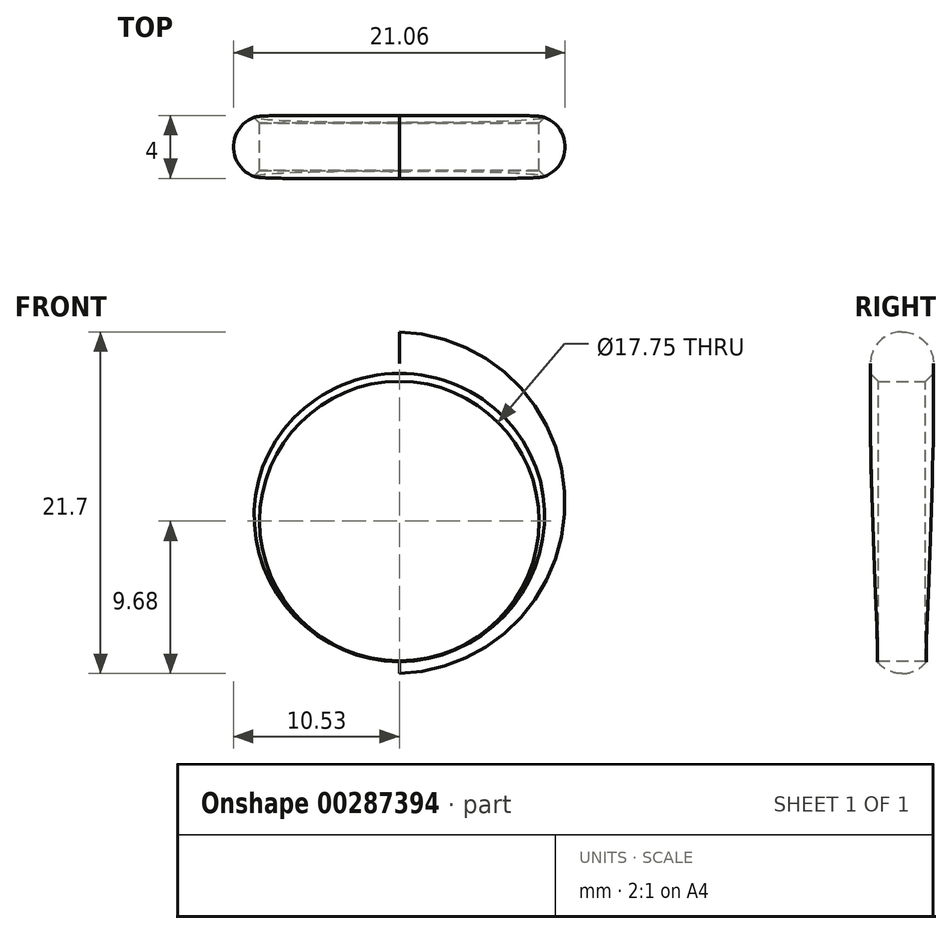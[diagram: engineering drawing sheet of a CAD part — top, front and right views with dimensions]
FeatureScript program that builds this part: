
annotation { "Feature Type Name" : "Feature", "Feature Type Description" : "" }
export const myFeature = defineFeature(function(context is Context, id is Id, definition is map)
    precondition{}
    {
        {
            var Q0;
            Q0=qCreatedBy(makeId("Front.planeOp"),FACE);
            var sketch = newSketch(context, id + "F0", { "sketchPlane" : qUnion([Q0])});
            skCircle(sketch, "E0", {"center": v(0, 0) * mm, "radius": 8.88 * mm});
            skPoint(sketch, "E1", {"position": v(0, 12.02) * mm});
            skPoint(sketch, "E2", {"position": v(0, -9.68) * mm});
            skArc(sketch, "E3", {"start": v(0, 12.02) * mm, "mid": v(-10.53, 1.17) * mm, "end": v(0, -9.68) * mm});
            skArc(sketch, "E4.MirrorCS", {"start": v(0, 12.02) * mm, "mid": v(10.53, 1.17) * mm, "end": v(0, -9.68) * mm});
            skPoint(sketch, "E5", {"position": v(-10.52, 10.9) * mm});
            skPoint(sketch, "E6", {"position": v(0, 15.2) * mm});
            skArc(sketch, "E7", {"start": v(0, 15.2) * mm, "mid": v(-5.65, 14) * mm, "end": v(-10.52, 10.9) * mm});
            skArc(sketch, "E8", {"start": v(-10.52, 10.9) * mm, "mid": v(-11.14, 8.31) * mm, "end": v(-9.01, 6.7) * mm});
            skArc(sketch, "E9.MirrorCS", {"start": v(0, 15.2) * mm, "mid": v(5.65, 14) * mm, "end": v(10.52, 10.9) * mm});
            skArc(sketch, "E10.MirrorCS", {"start": v(10.52, 10.9) * mm, "mid": v(11.14, 8.31) * mm, "end": v(9.01, 6.7) * mm});
            skSolve(sketch);
        }
        {
            var Q0;
            Q0=makeQuery(id+"F0.imprint","IMPRINT",FACE,{"disambiguationData":[TD([[makeQuery(id+"F0.imprint","IMPRINT",EDGE,{"derivedFrom":sQuery(id+"F0.wireOp",EDGE,"E0")}),-1.0]])]});
            extrude(context, id + "F1", {"entities" : qUnion([Q0]), "depth" : 2 * mm, "hasSecondDirection" : true, "secondDirectionOppositeDirection" : true, "secondDirectionDepth" : 2 * mm});
        }
        {
            var Q0;
            Q0=makeQuery(id+"F1.opExtrude","CAP_EDGE",EDGE,{"disambiguationData":[OSD([sQuery(id+"F0.wireOp",EDGE,"E0")])],"isStart":true});
            var Q1;
            Q1=makeQuery(id+"F1.opExtrude","CAP_EDGE",EDGE,{"disambiguationData":[OSD([sQuery(id+"F0.wireOp",EDGE,"E0")])],"isStart":false});
            chamfer(context, id + "F2", {"entities" : qUnion([Q0, Q1]), "width" : .5 * mm, "tangentPropagation" : true});
        }
        {
            var Q0;
            Q0=makeQuery(id+"F1.opExtrude","CAP_EDGE",EDGE,{"disambiguationData":[OSD([sQuery(id+"F0.wireOp",EDGE,"E4.MirrorCS")])],"isStart":true});
            var Q1;
            Q1=makeQuery(id+"F1.opExtrude","CAP_EDGE",EDGE,{"disambiguationData":[OSD([sQuery(id+"F0.wireOp",EDGE,"E3")])],"isStart":true});
            var Q2;
            Q2=makeQuery(id+"F1.opExtrude","CAP_EDGE",EDGE,{"disambiguationData":[OSD([sQuery(id+"F0.wireOp",EDGE,"E4.MirrorCS")])],"isStart":false});
            var Q3;
            Q3=makeQuery(id+"F1.opExtrude","CAP_EDGE",EDGE,{"disambiguationData":[OSD([sQuery(id+"F0.wireOp",EDGE,"E3")])],"isStart":false});
            fillet(context, id + "F3", {"entities" : qUnion([Q0, Q1, Q2, Q3]), "radius" : 2 * mm, "tangentPropagation" : true, "allowEdgeOverflow" : false});
        }
    });
